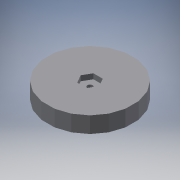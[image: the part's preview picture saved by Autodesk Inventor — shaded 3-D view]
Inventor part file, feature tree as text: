
AUTODESK INVENTOR PART (.ipt)
format: ipt  version: 2017 (Build 210142000, 142)  size: 127,488 bytes
history: native  units: mm
features: extrude x2, sketch x2
ambient origin geometry x8: Origin, YZ Plane, XZ Plane, XY Plane, X Axis, Y Axis, Z Axis, Center Point
bodies: Solid1 (feature_tree)
feature tree (4):
  extrude  "Extrusion1"  Depth=50.0mm TaperAngle=0.0deg
  extrude  "Extrusion2"  Depth=50.0mm
  sketch  "Sketch2"  dims[d0=260.0mm d1=50.0mm d2=0.0mm]
  sketch  "Sketch3"  dims[d3=16.0mm d4=50.0mm d5=16.0mm d6=0.0mm]
